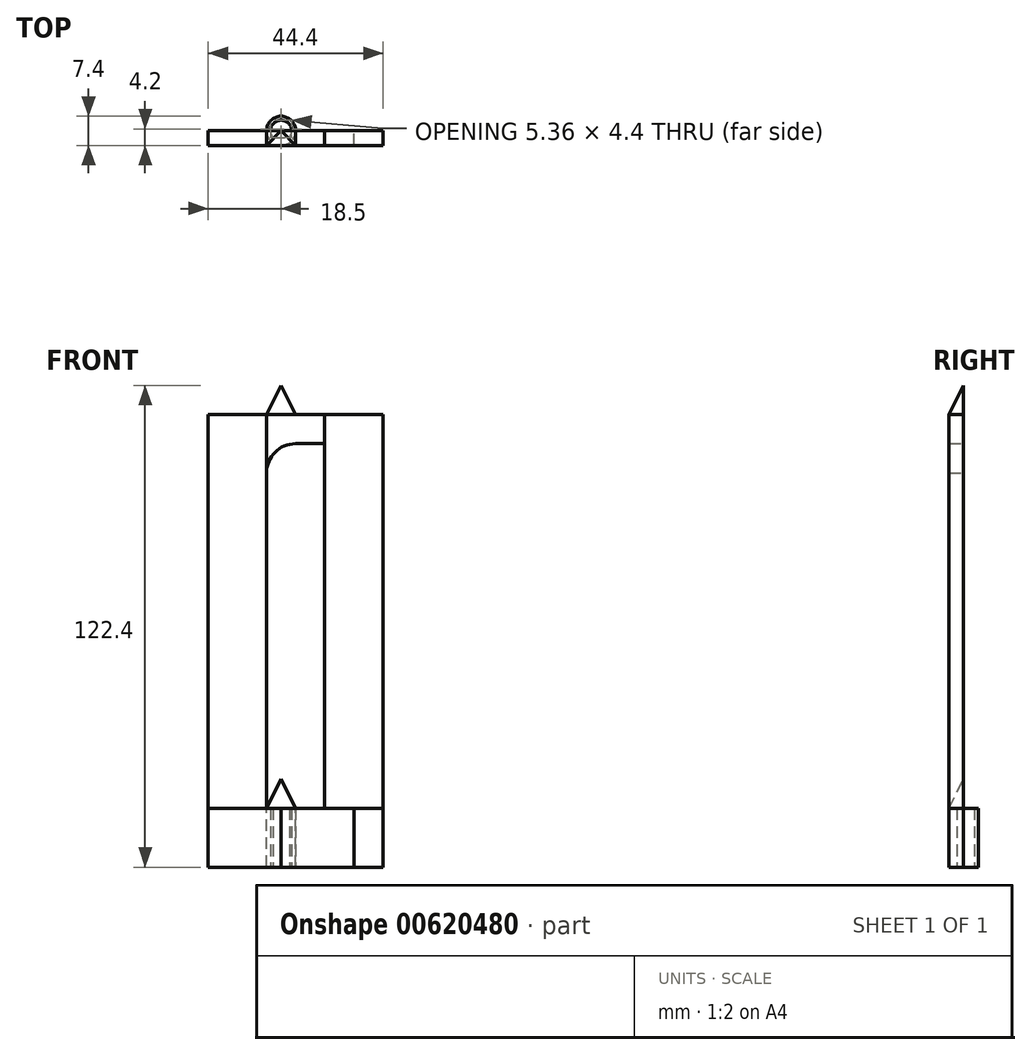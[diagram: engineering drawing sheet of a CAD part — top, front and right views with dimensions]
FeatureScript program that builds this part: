
annotation { "Feature Type Name" : "Feature", "Feature Type Description" : "" }
export const myFeature = defineFeature(function(context is Context, id is Id, definition is map)
    precondition{}
    {
        {
            var Q0;
            Q0=qCreatedBy(makeId("Top.planeOp"),FACE);
            var sketch = newSketch(context, id + "F0", { "sketchPlane" : qUnion([Q0])});
            skCircle(sketch, "E0", {"center": v(0, 0) * mm, "radius": 2.7 * mm});
            skLineSegment(sketch, "E1", {"start": v(0, 0) * mm, "end": v(0, -1.7) * mm});
            skLineSegment(sketch, "E2", {"start": v(0, -1.7) * mm, "end": v(2.1, -1.7) * mm});
            skLineSegment(sketch, "E3", {"start": v(0, -1.7) * mm, "end": v(-2.1, -1.7) * mm});
            skCircle(sketch, "E4", {"center": v(0, 0) * mm, "radius": 3.7 * mm});
            skSolve(sketch);
        }
        {
            var Q0;
            {var subQ0=sQuery(id+"F0.wireOp",EDGE,"E2");Q0=makeQuery(id+"F0.imprint","IMPRINT",FACE,{"disambiguationData":[TD([[makeQuery(id+"F0.imprint","IMPRINT",EDGE,{"derivedFrom":subQ0}),-1.0]])]});}
            var Q1;
            Q1=makeQuery(id+"F0.imprint","IMPRINT",FACE,{"disambiguationData":[TD([[makeQuery(id+"F0.imprint","IMPRINT",EDGE,{"derivedFrom":sQuery(id+"F0.wireOp",EDGE,"E4")}),1.0]])]});
            extrude(context, id + "F1", {"entities" : qUnion([Q0, Q1]), "depth" : 15 * mm, "offsetDistance" : 25 * mm});
        }
        {
            var Q0;
            Q0=makeQuery(id+"F1.opExtrude","CAP_FACE",FACE,{"disambiguationData":[OSD([sQuery(id+"F0.wireOp",EDGE,"E0"),sQuery(id+"F0.wireOp",EDGE,"E2"),sQuery(id+"F0.wireOp",EDGE,"E3"),sQuery(id+"F0.wireOp",EDGE,"E4")])],"isStart":false});
            var sketch = newSketch(context, id + "F2", { "sketchPlane" : qUnion([Q0])});
            skCircle(sketch, "E5", {"center": v(0, 0) * mm, "radius": 3.7 * mm});
            skLineSegment(sketch, "E6", {"start": v(0, 0) * mm, "end": v(3.7, 0) * mm});
            skLineSegment(sketch, "E7", {"start": v(3.7, 0) * mm, "end": v(-3.7, 0) * mm});
            skLineSegment(sketch, "E8", {"start": v(3.7, 0) * mm, "end": v(18.5, 0) * mm});
            skLineSegment(sketch, "E9", {"start": v(-3.7, 0) * mm, "end": v(-18.5, 0) * mm});
            skLineSegment(sketch, "E10", {"start": v(-18.5, 0) * mm, "end": v(-18.5, -3.7) * mm});
            skLineSegment(sketch, "E11", {"start": v(-18.5, -3.7) * mm, "end": v(18.5, -3.7) * mm});
            skLineSegment(sketch, "E12", {"start": v(18.5, -3.7) * mm, "end": v(18.5, 0) * mm});
            skLineSegment(sketch, "E13", {"start": v(3.7, 0) * mm, "end": v(3.7, -3.7) * mm});
            skLineSegment(sketch, "E14", {"start": v(-3.7, 0) * mm, "end": v(-3.7, -3.7) * mm});
            skSolve(sketch);
        }
        {
            var Q0;
            {var subQ0=sQuery(id+"F2.wireOp",EDGE,"E9");Q0=makeQuery(id+"F2.imprint","IMPRINT",FACE,{"disambiguationData":[TD([[makeQuery(id+"F2.imprint","IMPRINT",EDGE,{"derivedFrom":subQ0}),1.0]])]});}
            var Q1;
            {var subQ0=sQuery(id+"F2.wireOp",EDGE,"E8");Q1=makeQuery(id+"F2.imprint","IMPRINT",FACE,{"disambiguationData":[TD([[makeQuery(id+"F2.imprint","IMPRINT",EDGE,{"derivedFrom":subQ0}),-1.0]])]});}
            extrude(context, id + "F3", {"entities" : qUnion([Q0, Q1]), "operationType" : NewBodyOperationType.ADD, "depth" : 100 * mm, "offsetDistance" : 25 * mm});
        }
        {
            var Q0;
            {var subQ0=sQuery(id+"F2.wireOp",EDGE,"E14");Q0=makeQuery(id+"F2.imprint","IMPRINT",FACE,{"disambiguationData":[TD([[makeQuery(id+"F2.imprint","IMPRINT",EDGE,{"derivedFrom":subQ0}),1.0]])]});}
            var Q1;
            {var subQ0=sQuery(id+"F2.wireOp",EDGE,"E13");Q1=makeQuery(id+"F2.imprint","IMPRINT",FACE,{"disambiguationData":[TD([[makeQuery(id+"F2.imprint","IMPRINT",EDGE,{"derivedFrom":subQ0}),-1.0]])]});}
            var Q2;
            Q2=makeQuery(id+"F2.imprint","IMPRINT",FACE,{"disambiguationData":[TD([[makeQuery(id+"F2.imprint","IMPRINT",EDGE,{"derivedFrom":sQuery(id+"F2.wireOp",EDGE,"E8")}),-1.0]])]});
            var Q3;
            Q3=makeQuery(id+"F2.imprint","IMPRINT",FACE,{"disambiguationData":[TD([[makeQuery(id+"F2.imprint","IMPRINT",EDGE,{"derivedFrom":sQuery(id+"F2.wireOp",EDGE,"E9")}),1.0]])]});
            extrude(context, id + "F4", {"entities" : qUnion([Q0, Q1, Q2, Q3]), "oppositeDirection" : true, "depth" : 15 * mm, "offsetDistance" : 25 * mm});
        }
        {
            var Q0;
            Q0=makeQuery(id+"F3.opExtrude","SWEPT_EDGE",EDGE,{"disambiguationData":[OSD([sQuery(id+"F2.wireOp",EDGE,"E11"),sQuery(id+"F2.wireOp",EDGE,"E12")])]});
            var Q1;
            Q1=makeQuery(id+"F3.opExtrude","CAP_VERTEX",VERTEX,{"disambiguationData":[OSD([sQuery(id+"F2.wireOp",EDGE,"E11"),sQuery(id+"F2.wireOp",EDGE,"E12")])],"isStart":true});
            cPlane(context, id + "F5", {"entities" : qUnion([Q0, Q1]), "cplaneType" : CPlaneType.LINE_POINT, "offset" : 25 * mm, "width" : 150 * mm, "height" : 150 * mm});
        }
        {
            var Q0;
            Q0=qCreatedBy(makeId("Front.planeOp"),FACE);
            var sketch = newSketch(context, id + "F6", { "sketchPlane" : qUnion([Q0])});
            skPoint(sketch, "E15.0", {"position": v(3.7, 15) * mm});
            skPoint(sketch, "E16.0", {"position": v(0, 15) * mm});
            skPoint(sketch, "E17.0", {"position": v(-3.7, 15) * mm});
            skLineSegment(sketch, "E18", {"start": v(0, 15) * mm, "end": v(0, 22.4) * mm});
            skLineSegment(sketch, "E19", {"start": v(0, 22.4) * mm, "end": v(-3.7, 15) * mm});
            skLineSegment(sketch, "E20", {"start": v(0, 22.4) * mm, "end": v(3.7, 15) * mm});
            skLineSegment(sketch, "E21", {"start": v(3.7, 15) * mm, "end": v(-3.7, 15) * mm});
            skSolve(sketch);
        }
        {
            var Q0;
            Q0=qCreatedBy(id+"F5.planeOp",FACE);
            var sketch = newSketch(context, id + "F7", { "sketchPlane" : qUnion([Q0])});
            skPoint(sketch, "E22.0", {"position": v(-3.7, 0) * mm});
            skPoint(sketch, "E23.0", {"position": v(3.7, 3.7) * mm});
            skLineSegment(sketch, "E24.bottom", {"start": v(-3.7, 0) * mm, "end": v(3.7, 0) * mm});
            skLineSegment(sketch, "E24.top", {"start": v(-3.7, 3.7) * mm, "end": v(3.7, 3.7) * mm});
            skLineSegment(sketch, "E24.left", {"start": v(-3.7, 0) * mm, "end": v(-3.7, 3.7) * mm});
            skLineSegment(sketch, "E24.right", {"start": v(3.7, 0) * mm, "end": v(3.7, 3.7) * mm});
            skSolve(sketch);
        }
        {
            var Q0;
            Q0=makeQuery(id+"F7.imprint","IMPRINT",FACE,{"disambiguationData":[TD([[makeQuery(id+"F7.imprint","IMPRINT",EDGE,{"derivedFrom":sQuery(id+"F7.wireOp",EDGE,"E24.bottom")}),1.0]])]});
            var Q1;
            Q1=sQuery(id+"F6.wireOp",VERTEX,"E20.start");
            loft(context, id + "F8", {"sheetProfilesArray" : [{ "sheetProfileEntities" : qUnion([Q0]) }, { "sheetProfileEntities" : qUnion([Q1]) }]});
        }
        {
            var Q0;
            Q0=makeQuery(id+"F3.opExtrude","SWEPT_BODY",BODY,{"disambiguationData":[OSD([sQuery(id+"F2.wireOp",EDGE,"E8"),sQuery(id+"F2.wireOp",EDGE,"E11"),sQuery(id+"F2.wireOp",EDGE,"E12"),sQuery(id+"F2.wireOp",EDGE,"E13")])]});
            transform(context, id + "F9", {"entities" : qUnion([Q0]), "transformType" : TransformType.TRANSLATION_3D, "dx" : 7.4 * mm, "dy" : 0 * mm, "dz" : 0 * mm, "makeCopy" : false});
        }
        {
            var Q0;
            Q0=makeQuery(id+"F4.opExtrude","SWEPT_FACE",FACE,{"disambiguationData":[OSD([sQuery(id+"F2.wireOp",EDGE,"E12")])]});
            extrude(context, id + "F10", {"entities" : qUnion([Q0]), "depth" : 7.4 * mm, "offsetDistance" : 25 * mm});
        }
        {
            var Q0;
            Q0=qCreatedBy(makeId("Front.planeOp"),FACE);
            var sketch = newSketch(context, id + "F11", { "sketchPlane" : qUnion([Q0])});
            skPoint(sketch, "E25.0", {"position": v(-3.7, 115) * mm});
            skPoint(sketch, "E26.0", {"position": v(11.1, 115) * mm});
            skLineSegment(sketch, "E27", {"start": v(11.1, 115) * mm, "end": v(11.1, 107.6) * mm});
            skLineSegment(sketch, "E28", {"start": v(11.1, 107.6) * mm, "end": v(11.1, 100.2) * mm});
            skLineSegment(sketch, "E29.bottom", {"start": v(11.1, 100.2) * mm, "end": v(-3.7, 100.2) * mm});
            skLineSegment(sketch, "E29.top", {"start": v(11.1, 115) * mm, "end": v(-3.7, 115) * mm});
            skLineSegment(sketch, "E29.left", {"start": v(11.1, 100.2) * mm, "end": v(11.1, 115) * mm});
            skLineSegment(sketch, "E29.right", {"start": v(-3.7, 100.2) * mm, "end": v(-3.7, 115) * mm});
            skLineSegment(sketch, "E30", {"start": v(11.1, 107.6) * mm, "end": v(-3.7, 107.6) * mm});
            skArc(sketch, "E31", {"start": v(11.1, 100.2) * mm, "mid": v(3.7, 107.6) * mm, "end": v(-3.7, 100.2) * mm});
            skSolve(sketch);
        }
        {
            var Q0;
            {var subQ1=sQuery(id+"F11.wireOp",EDGE,"E29.top");Q0=makeQuery(id+"F11.imprint","IMPRINT",FACE,{"disambiguationData":[TD([[makeQuery(id+"F11.imprint","IMPRINT",EDGE,{"derivedFrom":subQ1}),1.0]])]});}
            var Q1;
            {var subQ1=sQuery(id+"F11.wireOp",EDGE,"E29.left");var subQ3=sQuery(id+"F11.wireOp",EDGE,"E30");var subQ4=makeQuery(id+"F11.imprint","INTERSECT",VERTEX,{"derivedFrom":[subQ1,subQ3]});Q1=makeQuery(id+"F11.imprint","IMPRINT",FACE,{"disambiguationData":[TD([[makeQuery(id+"F11.imprint","IMPRINT",EDGE,{"disambiguationData":[TD([[subQ4,-1.0]])],"derivedFrom":subQ3}),1.0]])]});}
            var Q2;
            {var subQ1=sQuery(id+"F11.wireOp",EDGE,"E29.right");var subQ3=sQuery(id+"F11.wireOp",EDGE,"E30");var subQ4=makeQuery(id+"F11.imprint","INTERSECT",VERTEX,{"derivedFrom":[subQ1,subQ3]});Q2=makeQuery(id+"F11.imprint","IMPRINT",FACE,{"disambiguationData":[TD([[makeQuery(id+"F11.imprint","IMPRINT",EDGE,{"disambiguationData":[TD([[subQ4,1.0]])],"derivedFrom":subQ3}),1.0]])]});}
            extrude(context, id + "F12", {"entities" : qUnion([Q0, Q1, Q2]), "depth" : 3.7 * mm, "offsetDistance" : 25 * mm});
        }
        {
            var Q0;
            Q0=makeQuery(id+"F8.opLoft","SWEPT_BODY",BODY,{"disambiguationData":[OSD([sQuery(id+"F6.wireOp",VERTEX,"E20.start"),makeQuery(id+"F7.imprint","IMPRINT",FACE,{"disambiguationData":[TD([[makeQuery(id+"F7.imprint","IMPRINT",EDGE,{"derivedFrom":sQuery(id+"F7.wireOp",EDGE,"E24.bottom")}),1.0]])]})])]});
            transform(context, id + "F13", {"entities" : qUnion([Q0]), "transformType" : TransformType.TRANSLATION_3D, "dx" : 0 * mm, "dy" : 0 * mm, "dz" : 100 * mm, "makeCopy" : true});
        }
    });
